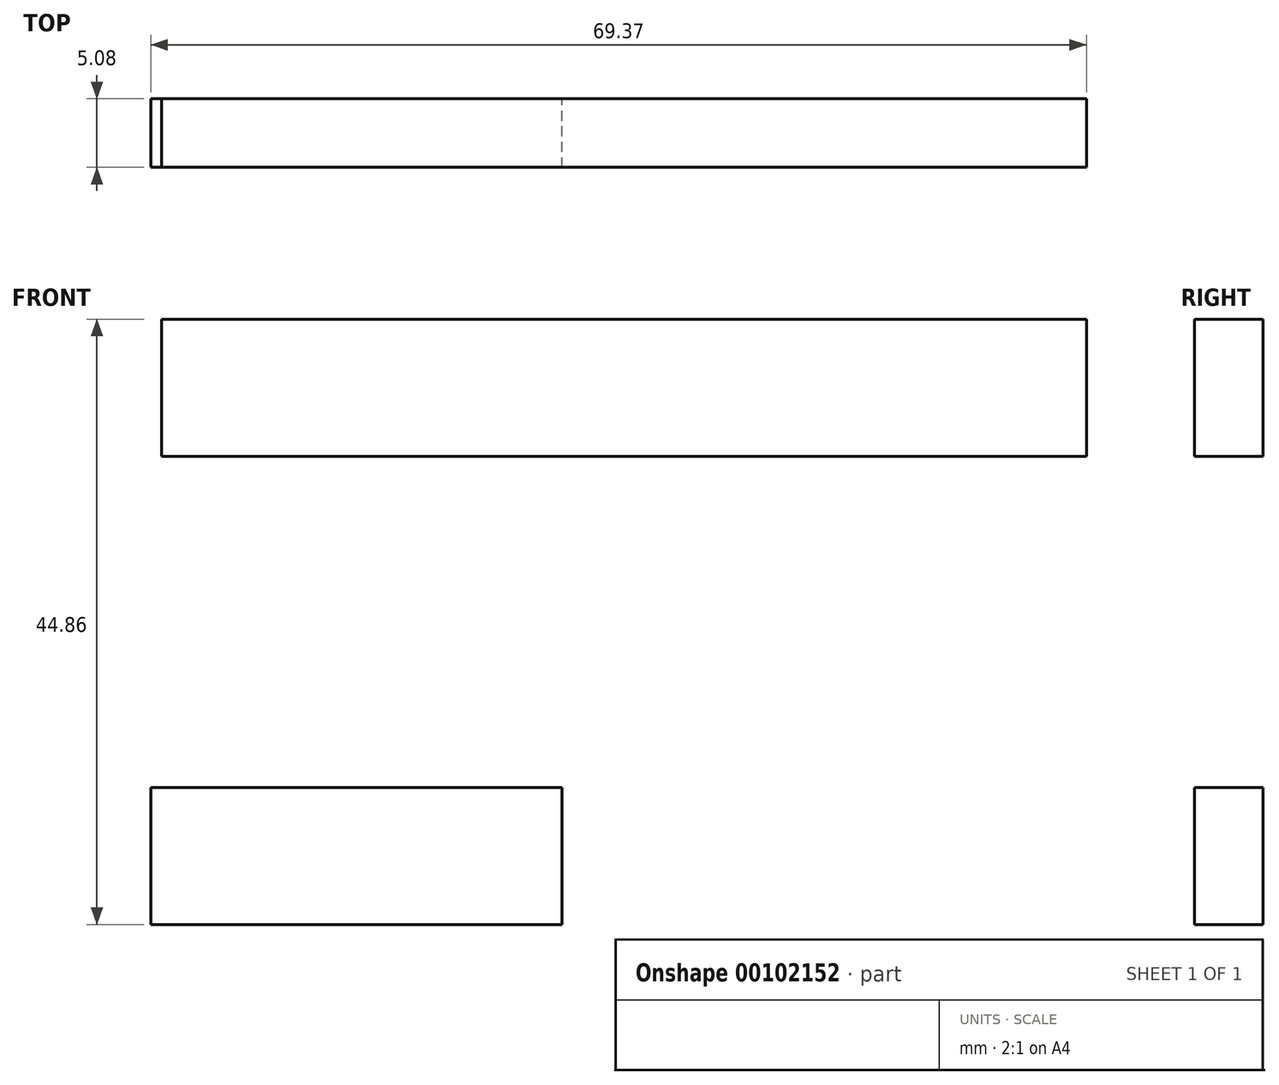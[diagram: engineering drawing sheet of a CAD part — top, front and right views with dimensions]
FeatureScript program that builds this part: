
annotation { "Feature Type Name" : "Feature", "Feature Type Description" : "" }
export const myFeature = defineFeature(function(context is Context, id is Id, definition is map)
    precondition{}
    {
        {
            var Q0;
            Q0=qCreatedBy(makeId("Front.planeOp"),FACE);
            var sketch = newSketch(context, id + "F0", { "sketchPlane" : qUnion([Q0])});
            skLineSegment(sketch, "E0.bottom", {"start": v(-57.89, 41.42) * mm, "end": v(10.7, 41.42) * mm});
            skLineSegment(sketch, "E0.top", {"start": v(-57.89, 31.26) * mm, "end": v(10.7, 31.26) * mm});
            skLineSegment(sketch, "E0.left", {"start": v(-57.89, 41.42) * mm, "end": v(-57.89, 31.26) * mm});
            skLineSegment(sketch, "E0.right", {"start": v(10.7, 41.42) * mm, "end": v(10.7, 31.26) * mm});
            skLineSegment(sketch, "E1.bottom", {"start": v(-58.68, 6.72) * mm, "end": v(-28.2, 6.72) * mm});
            skLineSegment(sketch, "E1.top", {"start": v(-58.68, -3.44) * mm, "end": v(-28.2, -3.44) * mm});
            skLineSegment(sketch, "E1.left", {"start": v(-58.68, 6.72) * mm, "end": v(-58.68, -3.44) * mm});
            skLineSegment(sketch, "E1.right", {"start": v(-28.2, 6.72) * mm, "end": v(-28.2, -3.44) * mm});
            skSolve(sketch);
        }
        {
            var Q0;
            Q0 = qSketchRegion(id + "F0", true);
            extrude(context, id + "F1", {"entities" : qUnion([Q0]), "depth" : 5.08 * mm});
        }
    });
